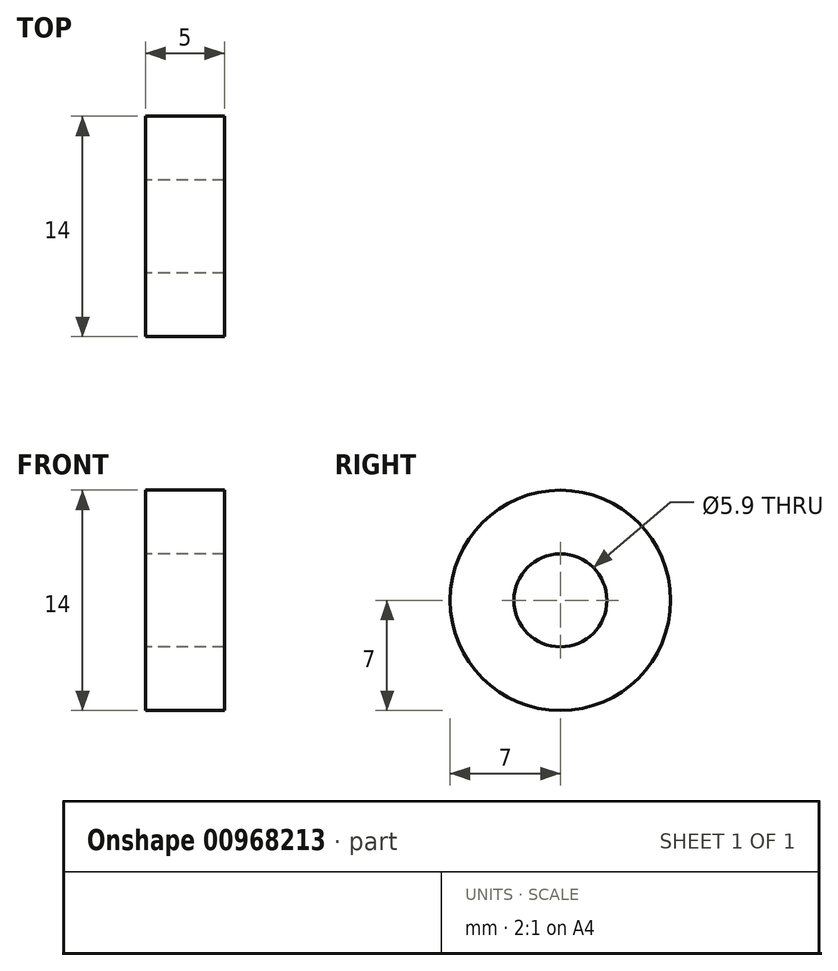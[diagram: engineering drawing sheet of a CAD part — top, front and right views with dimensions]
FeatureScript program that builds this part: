
annotation { "Feature Type Name" : "Feature", "Feature Type Description" : "" }
export const myFeature = defineFeature(function(context is Context, id is Id, definition is map)
    precondition{}
    {
        {
            var Q0;
            Q0=qCreatedBy(makeId("Right.planeOp"),FACE);
            var sketch = newSketch(context, id + "F0", { "sketchPlane" : qUnion([Q0])});
            skCircle(sketch, "E0", {"center": v(0, 0) * mm, "radius": 7 * mm});
            skCircle(sketch, "E1", {"center": v(0, 0) * mm, "radius": 2.95 * mm});
            skSolve(sketch);
        }
        {
            var Q0;
            Q0=makeQuery(id+"F0.imprint","IMPRINT",FACE,{"disambiguationData":[TD([[makeQuery(id+"F0.imprint","IMPRINT",EDGE,{"derivedFrom":sQuery(id+"F0.wireOp",EDGE,"E0")}),1.0]])]});
            extrude(context, id + "F1", {"entities" : qUnion([Q0]), "endBound" : BoundingType.SYMMETRIC, "depth" : 5 * mm, "offsetDistance" : 25 * mm});
        }
    });
